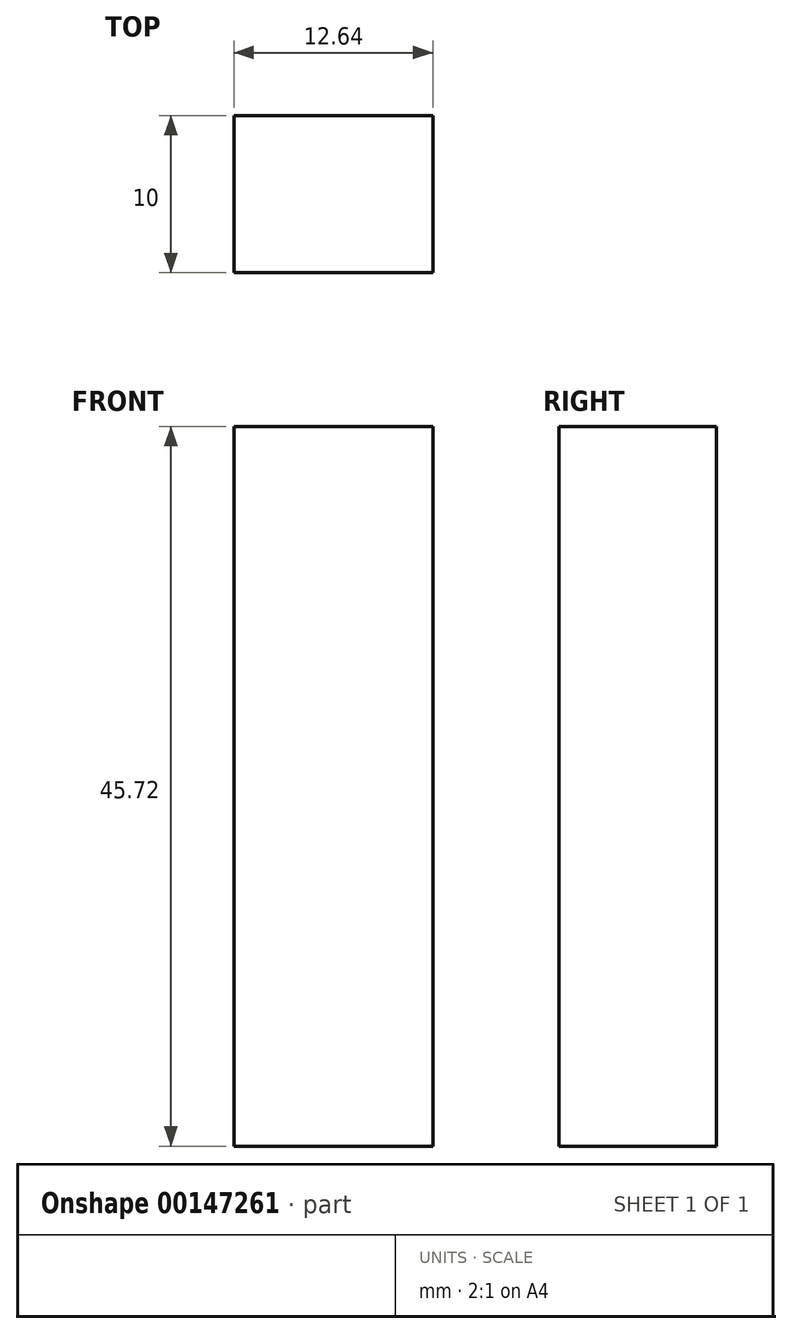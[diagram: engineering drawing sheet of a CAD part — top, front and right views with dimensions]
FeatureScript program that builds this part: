
annotation { "Feature Type Name" : "Feature", "Feature Type Description" : "" }
export const myFeature = defineFeature(function(context is Context, id is Id, definition is map)
    precondition{}
    {
        {
            var Q0;
            Q0=qCreatedBy(makeId("Top.planeOp"),FACE);
            var sketch = newSketch(context, id + "F0", { "sketchPlane" : qUnion([Q0])});
            skLineSegment(sketch, "E0.bottom", {"start": v(0, 0) * mm, "end": v(12.64, 0) * mm});
            skLineSegment(sketch, "E0.top", {"start": v(0, 10) * mm, "end": v(12.64, 10) * mm});
            skLineSegment(sketch, "E0.left", {"start": v(0, 0) * mm, "end": v(0, 10) * mm});
            skLineSegment(sketch, "E0.right", {"start": v(12.64, 0) * mm, "end": v(12.64, 10) * mm});
            skSolve(sketch);
        }
        {
            var Q0;
            Q0=makeQuery(id+"F0.imprint","IMPRINT",FACE,{"disambiguationData":[TD([[makeQuery(id+"F0.imprint","IMPRINT",EDGE,{"derivedFrom":sQuery(id+"F0.wireOp",EDGE,"E0.bottom")}),1.0]])]});
            extrude(context, id + "F1", {"entities" : qUnion([Q0]), "depth" : 45.72 * mm});
        }
    });
